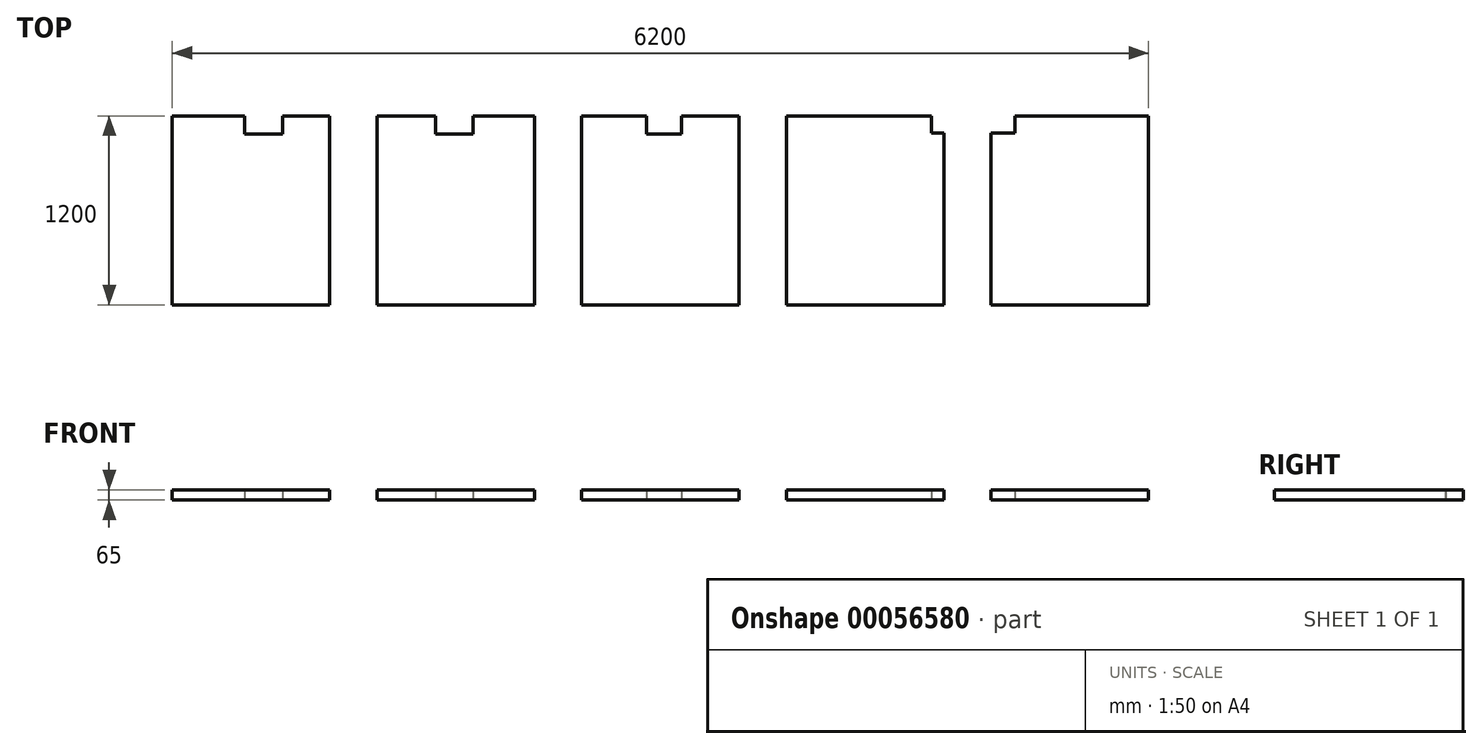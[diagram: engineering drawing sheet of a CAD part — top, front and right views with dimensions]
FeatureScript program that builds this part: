
annotation { "Feature Type Name" : "Feature", "Feature Type Description" : "" }
export const myFeature = defineFeature(function(context is Context, id is Id, definition is map)
    precondition{}
    {
        {
            var Q0;
            Q0=qCreatedBy(makeId("Top.planeOp"),FACE);
            var sketch = newSketch(context, id + "F0", { "sketchPlane" : qUnion([Q0])});
            skLineSegment(sketch, "E0.bottom", {"start": v(-569.27, 609.11) * mm, "end": v(-109.27, 609.11) * mm});
            skLineSegment(sketch, "E0.top", {"start": v(-569.27, -590.89) * mm, "end": v(430.73, -590.89) * mm});
            skLineSegment(sketch, "E0.left", {"start": v(-569.27, 609.11) * mm, "end": v(-569.27, -590.89) * mm});
            skLineSegment(sketch, "E0.right", {"start": v(430.73, 609.11) * mm, "end": v(430.73, -590.89) * mm});
            skLineSegment(sketch, "E1.top", {"start": v(-109.27, 494.11) * mm, "end": v(130.73, 494.11) * mm});
            skLineSegment(sketch, "E1.left", {"start": v(-109.27, 609.11) * mm, "end": v(-109.27, 494.11) * mm});
            skLineSegment(sketch, "E1.right", {"start": v(130.73, 609.11) * mm, "end": v(130.73, 494.11) * mm});
            skLineSegment(sketch, "E2.trimOffspring", {"start": v(130.73, 609.11) * mm, "end": v(430.73, 609.11) * mm});
            skLineSegment(sketch, "E3.bottom", {"start": v(730.73, 609.11) * mm, "end": v(1102.73, 609.11) * mm});
            skLineSegment(sketch, "E3.top", {"start": v(730.73, -590.89) * mm, "end": v(1730.73, -590.89) * mm});
            skLineSegment(sketch, "E3.left", {"start": v(730.73, 609.11) * mm, "end": v(730.73, -590.89) * mm});
            skLineSegment(sketch, "E3.right", {"start": v(1730.73, 609.11) * mm, "end": v(1730.73, -590.89) * mm});
            skLineSegment(sketch, "E4.top", {"start": v(1102.73, 494.11) * mm, "end": v(1342.73, 494.11) * mm});
            skLineSegment(sketch, "E4.left", {"start": v(1102.73, 609.11) * mm, "end": v(1102.73, 494.11) * mm});
            skLineSegment(sketch, "E4.right", {"start": v(1342.73, 609.11) * mm, "end": v(1342.73, 494.11) * mm});
            skLineSegment(sketch, "E5.trimOffspring", {"start": v(1342.73, 609.11) * mm, "end": v(1730.73, 609.11) * mm});
            skLineSegment(sketch, "E6.bottom", {"start": v(2030.73, 609.11) * mm, "end": v(2443.73, 609.11) * mm});
            skLineSegment(sketch, "E6.top", {"start": v(2030.73, -590.89) * mm, "end": v(3030.73, -590.89) * mm});
            skLineSegment(sketch, "E6.left", {"start": v(2030.73, 609.11) * mm, "end": v(2030.73, -590.89) * mm});
            skLineSegment(sketch, "E6.right", {"start": v(3030.73, 609.11) * mm, "end": v(3030.73, -590.89) * mm});
            skLineSegment(sketch, "E7.top", {"start": v(2443.73, 494.11) * mm, "end": v(2663.73, 494.11) * mm});
            skLineSegment(sketch, "E7.left", {"start": v(2443.73, 609.11) * mm, "end": v(2443.73, 494.11) * mm});
            skLineSegment(sketch, "E7.right", {"start": v(2663.73, 609.11) * mm, "end": v(2663.73, 494.11) * mm});
            skLineSegment(sketch, "E8.trimOffspring", {"start": v(2663.73, 609.11) * mm, "end": v(3030.73, 609.11) * mm});
            skLineSegment(sketch, "E9.bottom", {"start": v(3330.73, 609.11) * mm, "end": v(4252.73, 609.11) * mm});
            skLineSegment(sketch, "E9.top", {"start": v(3330.73, -590.89) * mm, "end": v(4330.73, -590.89) * mm});
            skLineSegment(sketch, "E9.left", {"start": v(3330.73, 609.11) * mm, "end": v(3330.73, -590.89) * mm});
            skLineSegment(sketch, "E9.right", {"start": v(4330.73, 499.11) * mm, "end": v(4330.73, -590.89) * mm});
            skLineSegment(sketch, "E10.top", {"start": v(4330.73, 499.11) * mm, "end": v(4252.73, 499.11) * mm});
            skLineSegment(sketch, "E10.right", {"start": v(4252.73, 609.11) * mm, "end": v(4252.73, 499.11) * mm});
            skPoint(sketch, "E11.firstSnap0", {"position": v(3791.73, 609.11) * mm});
            skLineSegment(sketch, "E11.bottom", {"start": v(4782.73, 609.11) * mm, "end": v(5630.73, 609.11) * mm});
            skLineSegment(sketch, "E11.top", {"start": v(4630.73, -590.89) * mm, "end": v(5630.73, -590.89) * mm});
            skLineSegment(sketch, "E11.left", {"start": v(4630.73, 499.11) * mm, "end": v(4630.73, -590.89) * mm});
            skLineSegment(sketch, "E11.right", {"start": v(5630.73, 609.11) * mm, "end": v(5630.73, -590.89) * mm});
            skLineSegment(sketch, "E12.top", {"start": v(4630.73, 499.11) * mm, "end": v(4782.73, 499.11) * mm});
            skLineSegment(sketch, "E12.right", {"start": v(4782.73, 609.11) * mm, "end": v(4782.73, 499.11) * mm});
            skSolve(sketch);
        }
        {
            var Q0;
            Q0 = qSketchRegion(id + "F0", true);
            extrude(context, id + "F1", {"entities" : qUnion([Q0]), "depth" : 65 * mm});
        }
    });
